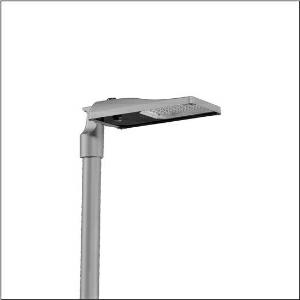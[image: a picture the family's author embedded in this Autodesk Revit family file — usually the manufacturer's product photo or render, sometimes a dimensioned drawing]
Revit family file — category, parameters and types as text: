
# Revit family: streetlight_sl_31_mini___p0_8a_5xh6u31t08ha_cf92
name_source: partatom
category: Lighting Fixtures
units: mm (PartAtom-declared; Revit-internal decimal feet)

## family parameters
Cut with Voids When Loaded = No
Host = Face
Light Source = No
Part Type = Normal
Room Calculation Point = No
Round Connector Dimension = Use Diameter
Shared = No

## types (1)
- --- (1 x LED, 9320 lm, 68.3 W, 3000K)
    Apparent Load = 68 VA
    CIE Flux Codes = 33 69 96 100 100
    Color Rendering = 70
    Color Temperature = 3000K
    Default Elevation = 1800 mm
    Description = Streetlight SL 31 mini D4i, Desk-Remote mast luminaire for post-top, side-entry; light control with lens of PMMA; light distribution: P0.8a, direct asymmetric distribution, for standard-compliant lighting for roads and squares; LED: luminous flux: 9.320lm, light colour: 730, colour temperature: 3000K; luminous efficacy: 136,5lm/W; control: pre-setting: logarithmic dimming characteristic, flexible luminous flux parameterisation, time-dependent luminous flux control, constant luminous flux control, power reduction, intelligent temperature release in ECG and LED module, overheat protection; luminaire housing, of diecast aluminium, Siteco® metallic grey (DB 702S), corrosivity category C5 high according to DIN EN ISO 12944; cover of toughened safety glass, transparent, opened without tools; mast flange of diecast aluminium, Siteco® metallic grey (DB 702S), spigot size: 76/60mm, mast flange included unmounted; with cable H07RN-F 2x 1.5mm², cable length: 8,5m, connection cable pre-assembled; mains connection: 220..240V, AC, 50/60Hz; power consumption (at start of service life): 68,3W / (at end of service life): 74,5W / (with reduced operation 50%): 29,5W; protection rating (complete): IP66; insulation class (complete): insulation class II (safety insulation); impact resistance: IK09; certification: CE, ENEC, ENEC+, VDE, UKCA, ZD4i; permissible operating ambient temperature for outdoor applications: -40..+50°C; packaging unit: 1 piece

Light Distribution: P0.8a
    Height = 76 mm
    Lamp = 1 x LED
    Lamp Light Flux = 9320 lm
    Lamp Power = 68.3 W
    Lamp count = 1
    Length = 547 mm
    Luminous efficacy = 136 lm/W
    Manufacturer = Siteco
    ModVariant = No
    Model = 5XH6U31T08HA
    Number of Poles = 1
    OnlyDefault = Yes
    Power Factor = 1
    Product Name = Streetlight SL 31 mini | P0.8a
    Product group = mast luminaire | pylon top
    ProductGroupID = 6100
    Protection Class = Protection class II
    Protection Degree = IP 66
    RLX_Detail_Level = 1
    RLX_Emergency_Light_Flux = 0 lm
    RLX_Emergency_Type = 0
    RLX_Emergency_Type_DB = No
    RlxData = <blob elided: 24109 chars, md5=92e4a5fa>
    Socket = socket
    Standby Power = 0 W
    System Light Flux = 9320 lm
    System Power = 68 W
    Type Comments = factory setting: luminous flux: 100 % | dim-lin: 254 | 692 mA
    Type Image = l_1300332.jpg
    URL = http://relux.com
    VarID = @adj_006605
    Voltage = 0 V
    Weight = 0.00 kg
    Width = 265 mm

## geometry (parser evidence)
native form markers: Blend x4, Sweep x10
no freeform markers — native parametric forms only
